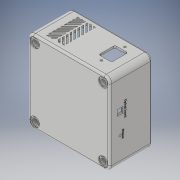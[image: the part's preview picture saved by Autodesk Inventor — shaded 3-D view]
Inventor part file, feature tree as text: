
AUTODESK INVENTOR PART (.ipt)
format: ipt  version: 2019 (Build 230136000, 136)  size: 2,727,936 bytes
history: native  units: mm
features: sketch x15, extrude x13, projected_geometry x11, other x5, fillet x4, reference x2, hole x1
ambient origin geometry x8: Origin, YZ Plane, XZ Plane, XY Plane, X Axis, Y Axis, Z Axis, Center Point
bodies: Body1 (feature_tree)
feature tree (51):
  other  "Твердое тело1"
  extrude  "Выдавливание1"  Depth=0.1mm
  extrude  "Выдавливание2"  Depth=0.3mm
  extrude  "Выдавливание3"  Depth=0.3mm
  fillet  "Сопряжение1"  Radius=0.3mm
  extrude  "Выдавливание5"  Depth=0.3mm
  extrude  "Выдавливание6"  Depth=2.1mm TaperAngle=0.0deg
  extrude  "Выдавливание7"  Depth=49.0mm TaperAngle=0.0deg
  extrude  "Выдавливание8"  Depth=2.5mm TaperAngle=0.0deg
  fillet  "Сопряжение2"  Radius=2.5mm
  fillet  "Сопряжение3"  Radius=12.0mm
  fillet  "Сопряжение4"  Radius=12.0mm
  extrude  "Выдавливание9"  Depth=12.0mm
  extrude  "Выдавливание10"  Depth=12.0mm
  extrude  "Выдавливание12"  Depth=1.4mm
  hole  "Отверстие1"  [1 undecoded]
  extrude  "Выдавливание13"  Depth=1.4mm
  extrude  "Выдавливание14"  Depth=1.4mm
  other  "Рельеф1"
  extrude  "Выдавливание15"  Depth=7.0mm
  sketch  "Эскиз1"
  reference  "Ссылка1"
  sketch  "Эскиз2"
  reference  "Ссылка2"
  projected_geometry  "Спроецированная петля1"
  sketch  "Эскиз3"
  projected_geometry  "Спроецированная петля2"
  sketch  "Эскиз4"
  sketch  "Эскиз5"
  sketch  "Эскиз6"
  sketch  "Эскиз7"
  sketch  "Эскиз8"
  sketch  "Эскиз9"
  sketch  "Эскиз10"
  projected_geometry  "Спроецированная петля3"
  sketch  "Эскиз11"
  sketch  "Эскиз13"
  sketch  "Эскиз15"
  sketch  "Эскиз16"
  projected_geometry  "Спроецированная петля5"
  projected_geometry  "Спроецированная петля6"
  projected_geometry  "Спроецированная петля7"
  projected_geometry  "Спроецированная петля8"
  projected_geometry  "Спроецированная петля9"
  projected_geometry  "Спроецированная петля10"
  projected_geometry  "Спроецированная петля11"
  projected_geometry  "Спроецированная петля12"
  sketch  "Эскиз17"
  other  "<userpath>\Documents\GitHub\Tesla_coil_V1\3dModels\TeslaCoil.iam"
  other  "TeslaCoil.iam"
  other  "TopBox:1"
note: 1 required parameter value undecoded (feature->parameter linkage not recoverable at this tier; creation-order binding heuristic only, values carry confidence <= 0.55)
